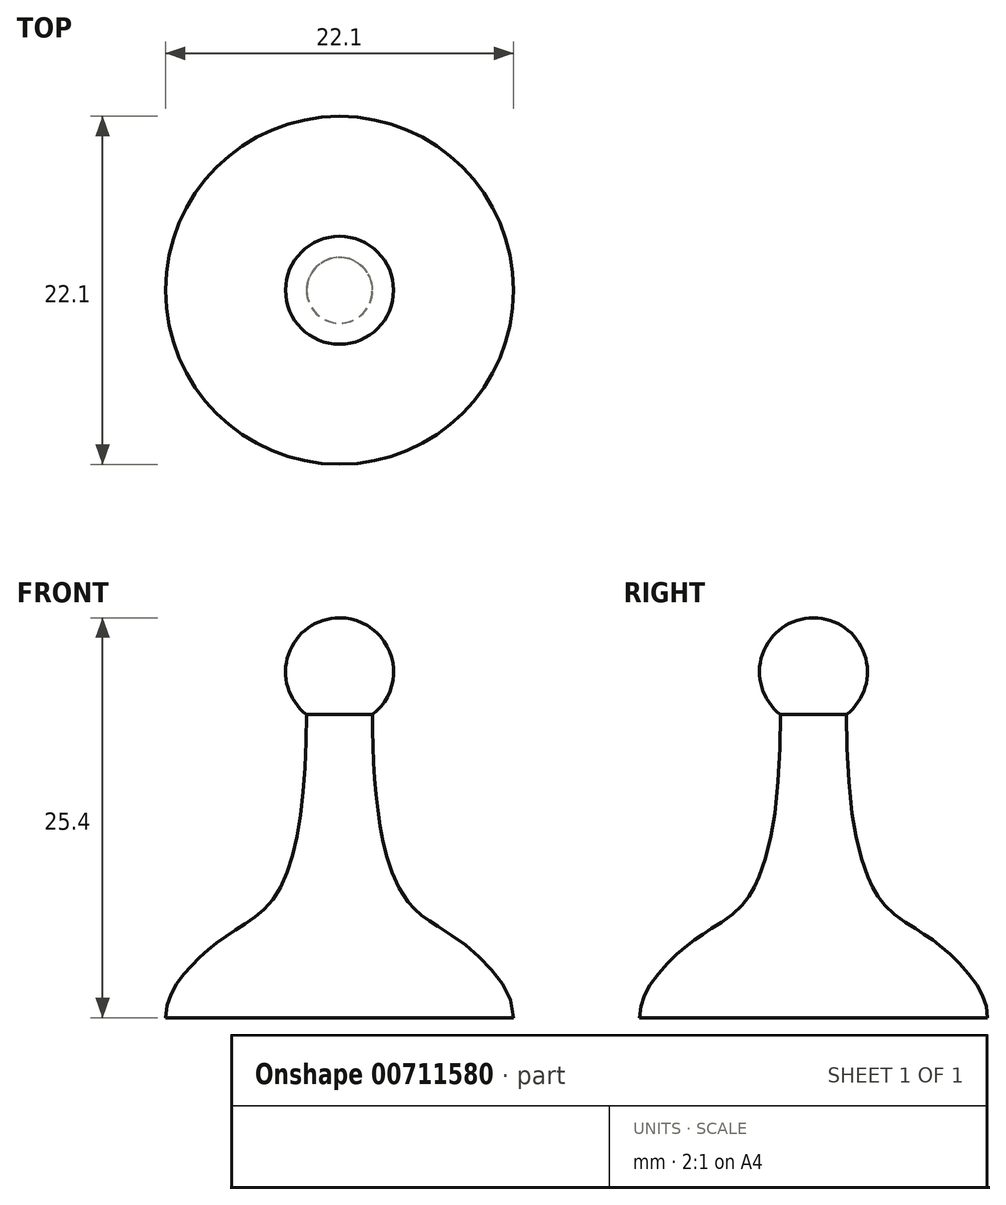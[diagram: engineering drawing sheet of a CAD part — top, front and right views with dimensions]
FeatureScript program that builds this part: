
annotation { "Feature Type Name" : "Feature", "Feature Type Description" : "" }
export const myFeature = defineFeature(function(context is Context, id is Id, definition is map)
    precondition{}
    {
        {
            var Q0;
            Q0=qCreatedBy(makeId("Front.planeOp"),FACE);
            var sketch = newSketch(context, id + "F0", { "sketchPlane" : qUnion([Q0])});
            skLineSegment(sketch, "E0", {"start": v(0, 21.97) * mm, "end": v(0, 0) * mm, "construction": true});
            skArc(sketch, "E1", {"start": v(2.1, 19.26) * mm, "mid": v(3.25, 23.08) * mm, "end": v(0, 25.4) * mm});
            skFitSpline(sketch, "E2", {"points": [v(2.1, 19.26) * mm, v(4.06, 7.75) * mm, v(6.99, 5.33) * mm, v(9.53, 3.18) * mm, v(11.05, 0) * mm], "startDerivative": vector(0, -40.43) * mm, "endDerivative": vector(0, -18.4) * mm});
            skLineSegment(sketch, "E3", {"start": v(11.05, 0) * mm, "end": v(0, 0) * mm});
            skLineSegment(sketch, "E4", {"start": v(0, 0) * mm, "end": v(0, 25.4) * mm});
            skSolve(sketch);
        }
        {
            var Q0;
            Q0=makeQuery(id+"F0.imprint","IMPRINT",FACE,{"disambiguationData":[TD([[makeQuery(id+"F0.imprint","IMPRINT",EDGE,{"derivedFrom":sQuery(id+"F0.wireOp",EDGE,"E1")}),1.0]])]});
            var Q1;
            Q1=sQuery(id+"F0.wireOp",EDGE,"E4");
            revolve(context, id + "F1", {"surfaceOperationType" : NewSurfaceOperationType.NEW, "entities" : qUnion([Q0]), "axis" : qUnion([Q1]), "revolveType" : RevolveType.FULL});
        }
    });
